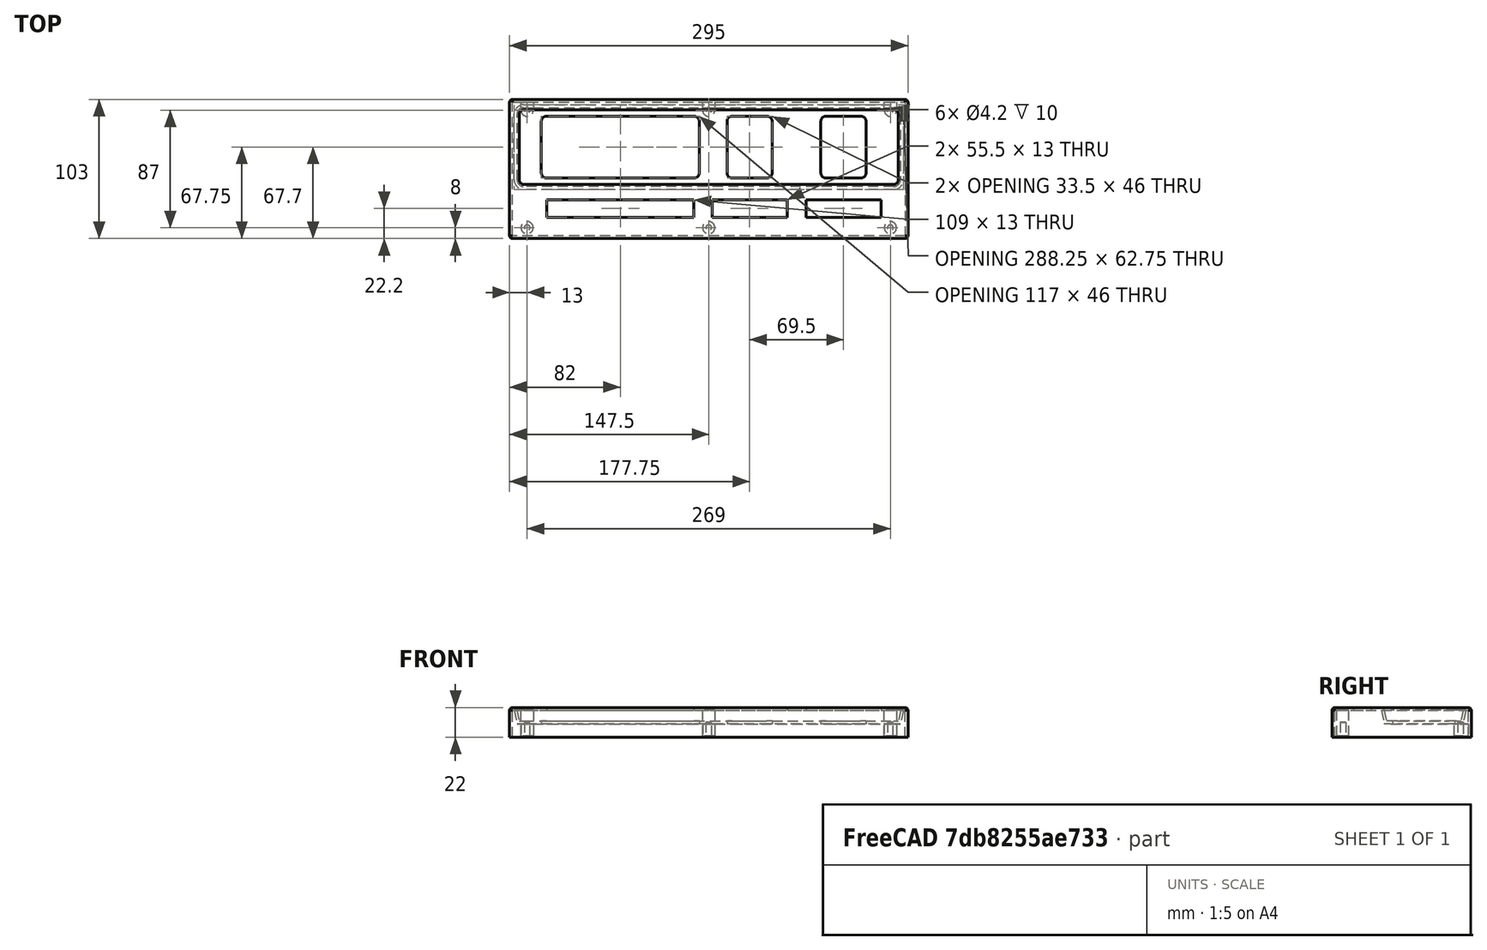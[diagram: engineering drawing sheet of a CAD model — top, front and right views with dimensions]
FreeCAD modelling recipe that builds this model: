
FCSTD DOCUMENT  (FreeCAD 0.21R33771 (Git))
Label: front panel
License: All rights reserved
LicenseURL: http://en.wikipedia.org/wiki/All_rights_reserved
objects: Sketcher::SketchObject×6, PartDesign::LinearPattern×4, PartDesign::Pad×3, PartDesign::Pocket×3, TechDraw::DrawViewDimension×3, PartDesign::Draft×1, PartDesign::Thickness×1, PartDesign::MultiTransform×1, PartDesign::Body×1, TechDraw::DrawSVGTemplate×1, TechDraw::DrawProjGroupItem×1, TechDraw::DrawProjGroup×1, TechDraw::DrawPage×1
note: 33 computed .brp shape members not serialized (recipe doc carries the construction recipe); baked Part::Feature solids carry a one-line shape summary decoded from their .brp

FEATURE [Sketcher::SketchObject] Sketch
  FullyConstrained = true
  MapMode = 5
  Support = -> [XY_Plane]
  sketch-geometry (4):
    g0: LineSegment StartX=-145.5 StartY=49.5 StartZ=0 EndX=145.5 EndY=49.5 EndZ=0
    g1: LineSegment StartX=145.5 StartY=49.5 StartZ=0 EndX=145.5 EndY=-49.5 EndZ=0
    g2: LineSegment StartX=145.5 StartY=-49.5 StartZ=0 EndX=-145.5 EndY=-49.5 EndZ=0
    g3: LineSegment StartX=-145.5 StartY=-49.5 StartZ=0 EndX=-145.5 EndY=49.5 EndZ=0
  constraints (11):
    c: Coincident(g0,g1)
    c: Coincident(g1,g2)
    c: Coincident(g2,g3)
    c: Coincident(g3,g0)
    c: Horizontal(g0)
    c: Horizontal(g2)
    c: Vertical(g1)
    c: Vertical(g3)
    c: Symmetric(g1,g0,g-1)
    c: DistanceY(g3,g3) = 99
    c: DistanceX(g0,g0) = 291
FEATURE [PartDesign::Pad] Pad
  Direction = (0,0,1)
  Length = 20
  Length2 = 10
  Profile = -> Sketch
  ReferenceAxis = -> Sketch [N_Axis]
  Type = 0
FEATURE [Sketcher::SketchObject] Sketch001
  FullyConstrained = true
  MapMode = 5
  Placement = pos=(0,0,20) rot=(0,0,1;0rad)
  Support = -> [Pad]
  sketch-geometry (10):
    g0: ArcOfCircle CenterX=-137 CenterY=40.5 CenterZ=0 NormalX=0 NormalY=0 NormalZ=1 AngleXU=0 Radius=5 StartAngle=1.5708 EndAngle=3.14159
    g1: LineSegment StartX=-137 StartY=45.5 StartZ=0 EndX=137 EndY=45.5 EndZ=0
    g2: ArcOfCircle CenterX=137 CenterY=40.5 CenterZ=0 NormalX=0 NormalY=0 NormalZ=1 AngleXU=0 Radius=5 StartAngle=5e-16 EndAngle=1.5708
    g3: LineSegment StartX=142 StartY=40.5 StartZ=0 EndX=142 EndY=-8 EndZ=0
    g4: ArcOfCircle CenterX=137 CenterY=-8 CenterZ=0 NormalX=0 NormalY=0 NormalZ=1 AngleXU=0 Radius=5 StartAngle=4.71239 EndAngle=6.28319
    g5: LineSegment StartX=137 StartY=-13 StartZ=0 EndX=-137 EndY=-13 EndZ=0
    g6: ArcOfCircle CenterX=-137 CenterY=-8 CenterZ=0 NormalX=0 NormalY=0 NormalZ=1 AngleXU=0 Radius=5 StartAngle=3.14159 EndAngle=4.71239
    g7: LineSegment StartX=-142 StartY=-8 StartZ=0 EndX=-142 EndY=40.5 EndZ=0
    g8: GeomPoint X=-142 Y=45.5 Z=0
    g9: GeomPoint X=142 Y=-13 Z=0
  constraints (23):
    c: Tangent(g0,g1) = 1.5708
    c: Tangent(g1,g2) = 1.5708
    c: Tangent(g2,g3) = 1.5708
    c: Tangent(g3,g4) = 1.5708
    c: Tangent(g4,g5) = 1.5708
    c: Tangent(g5,g6) = 1.5708
    c: Tangent(g6,g7) = 1.5708
    c: Tangent(g7,g0) = 1.5708
    c: Horizontal(g1)
    c: Horizontal(g5)
    c: Vertical(g3)
    c: Vertical(g7)
    c: Equal(g2,g4)
    c: Equal(g4,g6)
    c: PointOnObject(g8,g1)
    c: PointOnObject(g8,g7)
    c: PointOnObject(g9,g3)
    c: PointOnObject(g9,g5)
    c: Diameter(g2) = 10
    c: DistanceX(g0,g2) = 284
    c: Symmetric(g0,g2,g-2)
    c: DistanceY(g-1,g0) = 45.5
    c: DistanceY(g5,g-1) = 13
FEATURE [PartDesign::Pocket] Pocket
  BaseFeature = -> Pad
  Direction = (0,0,-1)
  Length = 10
  Length2 = 5
  Profile = -> Sketch001
  ReferenceAxis = -> Sketch001 [N_Axis]
  Type = 0
FEATURE [PartDesign::Draft] Draft
  Angle = 12
  Base = -> Pocket [Face10]
  BaseFeature = -> Pocket
  NeutralPlane = -> Pocket [Face15]
  SupportTransform = false
FEATURE [PartDesign::Thickness] Thickness
  Base = -> Draft [Face4]
  BaseFeature = -> Draft
  Intersection = false
  Join = 0
  Mode = 0
  SupportTransform = false
  Value = 2
FEATURE [Sketcher::SketchObject] Sketch002
  FullyConstrained = true
  MapMode = 5
  Placement = pos=(0,0,22) rot=(0,0,1;0rad)
  Support = -> [Thickness]
  sketch-geometry (42):
    g0: LineSegment StartX=-120 StartY=-22.8 StartZ=0 EndX=-11 EndY=-22.8 EndZ=0
    g1: LineSegment StartX=-11 StartY=-22.8 StartZ=0 EndX=-11 EndY=-35.8 EndZ=0
    g2: LineSegment StartX=-11 StartY=-35.8 StartZ=0 EndX=-120 EndY=-35.8 EndZ=0
    g3: LineSegment StartX=-120 StartY=-35.8 StartZ=0 EndX=-120 EndY=-22.8 EndZ=0
    g4: LineSegment StartX=2.5 StartY=-22.8 StartZ=0 EndX=58 EndY=-22.8 EndZ=0
    g5: LineSegment StartX=58 StartY=-22.8 StartZ=0 EndX=58 EndY=-35.8 EndZ=0
    g6: LineSegment StartX=58 StartY=-35.8 StartZ=0 EndX=2.5 EndY=-35.8 EndZ=0
    g7: LineSegment StartX=2.5 StartY=-35.8 StartZ=0 EndX=2.5 EndY=-22.8 EndZ=0
    g8: LineSegment StartX=72 StartY=-22.8 StartZ=0 EndX=127.5 EndY=-22.8 EndZ=0
    g9: LineSegment StartX=127.5 StartY=-22.8 StartZ=0 EndX=127.5 EndY=-35.8 EndZ=0
    g10: LineSegment StartX=127.5 StartY=-35.8 StartZ=0 EndX=72 EndY=-35.8 EndZ=0
    g11: LineSegment StartX=72 StartY=-35.8 StartZ=0 EndX=72 EndY=-22.8 EndZ=0
    g12: ArcOfCircle CenterX=-120 CenterY=35.2 CenterZ=0 NormalX=0 NormalY=0 NormalZ=1 AngleXU=0 Radius=4 StartAngle=1.5708 EndAngle=3.14159
    g13: LineSegment StartX=-120 StartY=39.2 StartZ=0 EndX=-11 EndY=39.2 EndZ=0
    g14: ArcOfCircle CenterX=-11 CenterY=35.2 CenterZ=0 NormalX=0 NormalY=0 NormalZ=1 AngleXU=0 Radius=4 StartAngle=1e-16 EndAngle=1.5708
    g15: LineSegment StartX=-7 StartY=35.2 StartZ=0 EndX=-7 EndY=-2.8 EndZ=0
    g16: ArcOfCircle CenterX=-11 CenterY=-2.8 CenterZ=0 NormalX=0 NormalY=0 NormalZ=1 AngleXU=0 Radius=4 StartAngle=4.71239 EndAngle=6.28319
    g17: LineSegment StartX=-11 StartY=-6.8 StartZ=0 EndX=-120 EndY=-6.8 EndZ=0
    g18: ArcOfCircle CenterX=-120 CenterY=-2.8 CenterZ=0 NormalX=0 NormalY=0 NormalZ=1 AngleXU=0 Radius=4 StartAngle=3.14159 EndAngle=4.71239
    g19: LineSegment StartX=-124 StartY=-2.8 StartZ=0 EndX=-124 EndY=35.2 EndZ=0
    g20: GeomPoint X=-124 Y=39.2 Z=0
    g21: GeomPoint X=-7 Y=-6.8 Z=0
    g22: ArcOfCircle CenterX=17.5 CenterY=35.2 CenterZ=0 NormalX=0 NormalY=0 NormalZ=1 AngleXU=0 Radius=4 StartAngle=1.5708 EndAngle=3.14159
    g23: LineSegment StartX=17.5 StartY=39.2 StartZ=0 EndX=43 EndY=39.2 EndZ=0
    g24: ArcOfCircle CenterX=43 CenterY=35.2 CenterZ=0 NormalX=0 NormalY=0 NormalZ=1 AngleXU=0 Radius=4 StartAngle=0 EndAngle=1.5708
    g25: LineSegment StartX=47 StartY=35.2 StartZ=0 EndX=47 EndY=-2.8 EndZ=0
    g26: ArcOfCircle CenterX=43 CenterY=-2.8 CenterZ=0 NormalX=0 NormalY=0 NormalZ=1 AngleXU=0 Radius=4 StartAngle=4.71239 EndAngle=6.28319
    g27: LineSegment StartX=43 StartY=-6.8 StartZ=0 EndX=17.5 EndY=-6.8 EndZ=0
    g28: ArcOfCircle CenterX=17.5 CenterY=-2.8 CenterZ=0 NormalX=0 NormalY=0 NormalZ=1 AngleXU=0 Radius=4 StartAngle=3.14159 EndAngle=4.71239
    g29: LineSegment StartX=13.5 StartY=-2.8 StartZ=0 EndX=13.5 EndY=35.2 EndZ=0
    g30: GeomPoint X=13.5 Y=39.2 Z=0
    g31: GeomPoint X=47 Y=-6.8 Z=0
    g32: ArcOfCircle CenterX=87 CenterY=35.2 CenterZ=0 NormalX=0 NormalY=0 NormalZ=1 AngleXU=0 Radius=4 StartAngle=1.5708 EndAngle=3.14159
    g33: LineSegment StartX=87 StartY=39.2 StartZ=0 EndX=112.5 EndY=39.2 EndZ=0
    g34: ArcOfCircle CenterX=112.5 CenterY=35.2 CenterZ=0 NormalX=0 NormalY=0 NormalZ=1 AngleXU=0 Radius=4 StartAngle=1e-16 EndAngle=1.5708
    g35: LineSegment StartX=116.5 StartY=35.2 StartZ=0 EndX=116.5 EndY=-2.8 EndZ=0
    g36: ArcOfCircle CenterX=112.5 CenterY=-2.8 CenterZ=0 NormalX=0 NormalY=0 NormalZ=1 AngleXU=0 Radius=4 StartAngle=4.71239 EndAngle=6.28319
    g37: LineSegment StartX=112.5 StartY=-6.8 StartZ=0 EndX=87 EndY=-6.8 EndZ=0
    g38: ArcOfCircle CenterX=87 CenterY=-2.8 CenterZ=0 NormalX=0 NormalY=0 NormalZ=1 AngleXU=0 Radius=4 StartAngle=3.14159 EndAngle=4.71239
    g39: LineSegment StartX=83 StartY=-2.8 StartZ=0 EndX=83 EndY=35.2 EndZ=0
    g40: GeomPoint X=83 Y=39.2 Z=0
    g41: GeomPoint X=116.5 Y=-6.8 Z=0
  constraints (108):
    c: Coincident(g0,g1)
    c: Coincident(g1,g2)
    c: Coincident(g2,g3)
    c: Coincident(g3,g0)
    c: Horizontal(g0)
    c: Horizontal(g2)
    c: Vertical(g1)
    c: Vertical(g3)
    c: Coincident(g4,g5)
    c: Coincident(g5,g6)
    c: Coincident(g6,g7)
    c: Coincident(g7,g4)
    c: Horizontal(g4)
    c: Horizontal(g6)
    c: Vertical(g5)
    c: Vertical(g7)
    c: Coincident(g8,g9)
    c: Coincident(g9,g10)
    c: Coincident(g10,g11)
    c: Coincident(g11,g8)
    c: Horizontal(g8)
    c: Horizontal(g10)
    c: Vertical(g9)
    c: Vertical(g11)
    c: Horizontal(g10,g5)
    c: Horizontal(g5,g1)
    c: Horizontal(g4,g0)
    c: Horizontal(g0,g8)
    c: DistanceY(g3,g3) = 13
    c: DistanceX(g2,g-1) = 120
    c: DistanceX(g0,g0) = 109
    c: DistanceY(g1,g-1) = 35.8
    c: DistanceX(g0,g4) = 13.5
    c: DistanceX(g4,g4) = 55.5
    c: DistanceX(g4,g8) = 14
    c: Equal(g8,g4)
    c: Tangent(g12,g13) = 1.5708
    c: Tangent(g13,g14) = 1.5708
    c: Tangent(g14,g15) = 1.5708
    c: Tangent(g15,g16) = 1.5708
    c: Tangent(g16,g17) = 1.5708
    c: Tangent(g17,g18) = 1.5708
    c: Tangent(g18,g19) = 1.5708
    c: Tangent(g19,g12) = 1.5708
    c: Horizontal(g13)
    c: Horizontal(g17)
    c: Vertical(g15)
    c: Vertical(g19)
    c: Equal(g12,g14)
    c: Equal(g14,g16)
    c: Equal(g16,g18)
    c: PointOnObject(g20,g13)
    c: PointOnObject(g20,g19)
    c: PointOnObject(g21,g15)
    c: PointOnObject(g21,g17)
    c: Radius(g12) = 4
    c: Vertical(g17,g0)
    c: Vertical(g16,g0)
    c: Tangent(g22,g23) = 1.5708
    c: Tangent(g23,g24) = 1.5708
    c: Tangent(g24,g25) = 1.5708
    c: Tangent(g25,g26) = 1.5708
    c: Tangent(g26,g27) = 1.5708
    c: Tangent(g27,g28) = 1.5708
    c: Tangent(g28,g29) = 1.5708
    c: Tangent(g29,g22) = 1.5708
    c: Horizontal(g23)
    c: Horizontal(g27)
    c: Vertical(g25)
    c: Vertical(g29)
    c: Equal(g22,g24)
    c: Equal(g24,g26)
    c: Equal(g26,g28)
    c: PointOnObject(g30,g23)
    c: PointOnObject(g30,g29)
    c: PointOnObject(g31,g25)
    c: PointOnObject(g31,g27)
    c: Equal(g26,g14)
    c: Horizontal(g22,g13)
    c: Horizontal(g27,g16)
    c: DistanceX(g26,g4) = 15
    c: DistanceX(g4,g27) = 15
    c: Tangent(g32,g33) = 1.5708
    c: Tangent(g33,g34) = 1.5708
    c: Tangent(g34,g35) = 1.5708
    c: Tangent(g35,g36) = 1.5708
    c: Tangent(g36,g37) = 1.5708
    c: Tangent(g37,g38) = 1.5708
    c: Tangent(g38,g39) = 1.5708
    c: Tangent(g39,g32) = 1.5708
    c: Horizontal(g33)
    c: Horizontal(g37)
    c: Vertical(g35)
    c: Vertical(g39)
    c: Equal(g32,g34)
    c: Equal(g34,g36)
    c: Equal(g36,g38)
    c: PointOnObject(g40,g33)
    c: PointOnObject(g40,g39)
    c: PointOnObject(g41,g35)
    c: PointOnObject(g41,g37)
    c: Horizontal(g23,g32)
    c: Equal(g32,g24)
    c: DistanceX(g36,g8) = 15
    c: Equal(g27,g37)
    c: DistanceY(g8,g35) = 20
    c: DistanceY(g8,g33) = 62
    c: Horizontal(g37,g16)
FEATURE [PartDesign::Pocket] Pocket001
  BaseFeature = -> Thickness
  Direction = (0,0,-1)
  Length = 5
  Length2 = 5
  Profile = -> Sketch002
  ReferenceAxis = -> Sketch002 [N_Axis]
  Type = 1
FEATURE [Sketcher::SketchObject] Sketch003
  FullyConstrained = true
  MapMode = 5
  Placement = pos=(0,0,20) rot=(1,0,0;3.14159rad)
  Support = -> [Pocket001]
  sketch-geometry (1):
    g0: Circle CenterX=-134.5 CenterY=43.5 CenterZ=0 NormalX=0 NormalY=0 NormalZ=1 AngleXU=0 Radius=4.5
  constraints (3):
    c: DistanceY(g-1,g0) = 43.5
    c: DistanceX(g0,g-1) = 134.5
    c: Diameter(g0) = 9
FEATURE [PartDesign::Pad] Pad001
  BaseFeature = -> Pocket001
  Direction = (0,0,-1)
  Length = 19
  Length2 = 10
  Profile = -> Sketch003
  ReferenceAxis = -> Sketch003 [N_Axis]
  Type = 0
FEATURE [PartDesign::LinearPattern] LinearPattern
  BaseFeature = -> Pad001
  Direction = -> Sketch003 [H_Axis]
  Length = 269
  Occurrences = 3
  Originals = -> [Pad001]
FEATURE [Sketcher::SketchObject] Sketch004
  ExternalGeometry = -> [LinearPattern]
  FullyConstrained = true
  MapMode = 5
  Placement = pos=(0,0,10) rot=(1,0,0;3.14159rad)
  Support = -> [LinearPattern]
  sketch-geometry (4):
    g0: ArcOfCircle CenterX=-134.5 CenterY=-43.5 CenterZ=0 NormalX=0 NormalY=0 NormalZ=1 AngleXU=0 Radius=4.5 StartAngle=-9e-16 EndAngle=3.14159
    g1: LineSegment StartX=-139 StartY=-43.5 StartZ=0 EndX=-139 EndY=-49.5 EndZ=0
    g2: LineSegment StartX=-139 StartY=-49.5 StartZ=0 EndX=-130 EndY=-49.5 EndZ=0
    g3: LineSegment StartX=-130 StartY=-49.5 StartZ=0 EndX=-130 EndY=-43.5 EndZ=0
  constraints (11):
    c: Tangent(g0,g1) = -1.5708
    c: Coincident(g1,g2)
    c: PointOnObject(g2,g-3)
    c: Horizontal(g2)
    c: Coincident(g2,g3)
    c: Vertical(g3)
    c: Vertical(g1)
    c: Diameter(g0) = 9
    c: DistanceX(g0,g-1) = 134.5
    c: DistanceY(g0,g-1) = 43.5
    c: Tangent(g3,g0) = -1.5708
FEATURE [PartDesign::Pad] Pad002
  BaseFeature = -> LinearPattern
  Direction = (0,0,-1)
  Length = 9
  Length2 = 10
  Profile = -> Sketch004
  ReferenceAxis = -> Sketch004 [N_Axis]
  Type = 0
FEATURE [PartDesign::LinearPattern] LinearPattern001
  BaseFeature = -> Pad002
  Direction = -> Sketch004 [H_Axis]
  Length = 269
  Occurrences = 3
  Originals = -> [Pad002]
FEATURE [Sketcher::SketchObject] Sketch005
  ExternalGeometry = -> [LinearPattern001]
  FullyConstrained = true
  MapMode = 5
  Placement = pos=(0,0,1) rot=(1,0,0;3.14159rad)
  Support = -> [LinearPattern001]
  sketch-geometry (1):
    g0: Circle CenterX=-134.5 CenterY=43.5 CenterZ=0 NormalX=0 NormalY=0 NormalZ=1 AngleXU=0 Radius=2.1
  constraints (2):
    c: Coincident(g0,g-3)
    c: Diameter(g0) = 4.2
FEATURE [PartDesign::Pocket] Pocket002
  BaseFeature = -> LinearPattern001
  Direction = (0,0,1)
  Length = 10
  Length2 = 5
  Profile = -> Sketch005
  ReferenceAxis = -> Sketch005 [N_Axis]
  Type = 0
FEATURE [PartDesign::LinearPattern] LinearPattern002
  Direction = -> Sketch005 [H_Axis]
  Length = 269
  Occurrences = 3
FEATURE [PartDesign::LinearPattern] LinearPattern003
  Direction = -> Sketch005 [V_Axis]
  Length = 87
  Occurrences = 2
  Reversed = true
FEATURE [PartDesign::MultiTransform] MultiTransform
  BaseFeature = -> Pocket002
  Originals = -> [Pocket002]
  Transformations = -> [LinearPattern002,LinearPattern003]
FEATURE [PartDesign::Body] Body
  Group = -> [Sketch,Pad,Sketch001,Pocket,Draft,Thickness,Sketch002,Pocket001,Sketch003,Pad001,LinearPattern,Sketch004,Pad002,LinearPattern001,Sketch005,Pocket002,MultiTransform,LinearPattern002,LinearPattern003]
  Origin = -> Origin
  Tip = -> MultiTransform
FEATURE [TechDraw::DrawSVGTemplate] Template
  EditableTexts = APPROVER_NAME=APPROVER NAME; AUTHOR_NAME=AUTHOR NAME; DATE=YYYY-MM-DD; DN=DN; DOCUMENT_TYPE=Mechanical assembly drawing; OWNER_NAME=OWNER NAME; PM=PM; PN=PN; REVISION=REV A; RIGHTS=(R) DO NOT DUPLICATE THIS DRAWING TO THIRD PARTIES WITHOUT OWNER'S PERMISSION!; SCALE=M x:x; SHEET=99 of 99; SIZE=A3; TITLELINE-1=FreeCAD; TOLERANCE=+/- ?
  Height = 297
  Orientation = 1
  Template = /Applications/FreeCAD.app/Contents/Resources/share/Mod/TechDraw/Templates/A3_Landscape_ISO7200_Pep.svg
  Width = 420
FEATURE [TechDraw::DrawProjGroupItem] ProjItem  label="Front"
  CoarseView = false
  Direction = (0,0,1)
  Focus = 100
  HardHidden = false
  IsoCount = 0
  IsoHidden = false
  IsoVisible = false
  LockPosition = true
  Perspective = false
  Rotation = 0
  RotationVector = (1,0,0)
  ScaleType = 2
  ScrubCount = 0
  SeamHidden = false
  SeamVisible = true
  SmoothHidden = false
  SmoothVisible = true
  Source = -> [Body]
  Type = 0
  X = 0
  XDirection = (1,0,0)
  Y = 0
FEATURE [TechDraw::DrawProjGroup] ProjGroup
  Anchor = -> ProjItem
  AutoDistribute = true
  LockPosition = false
  ProjectionType = 0
  Rotation = 0
  ScaleType = 0
  Source = -> [Body]
  Views = -> [ProjItem]
  X = 210
  Y = 148.5
  spacingX = 15
  spacingY = 15
FEATURE [TechDraw::DrawViewDimension] Dimension
  AngleOverride = false
  Arbitrary = false
  ArbitraryTolerances = false
  EqualTolerance = true
  ExtensionAngle = 0
  FormatSpec = %.3f
  FormatSpecOverTolerance = %+.3f
  FormatSpecUnderTolerance = %+.3f
  Inverted = false
  LineAngle = 0
  LockPosition = false
  MeasureType = 1
  OverTolerance = 0
  References2D = -> [ProjItem]
  Rotation = 0
  ScaleType = 0
  TheoreticalExact = false
  Type = 1
  UnderTolerance = 0
  X = -2.31406
  Y = 78.7935
FEATURE [TechDraw::DrawViewDimension] Dimension001
  AngleOverride = false
  Arbitrary = false
  ArbitraryTolerances = false
  EqualTolerance = true
  ExtensionAngle = 0
  FormatSpec = %.3f
  FormatSpecOverTolerance = %+.3f
  FormatSpecUnderTolerance = %+.3f
  Inverted = false
  LineAngle = 0
  LockPosition = false
  MeasureType = 1
  OverTolerance = 0
  References2D = -> [ProjItem]
  Rotation = 0
  ScaleType = 0
  TheoreticalExact = false
  Type = 2
  UnderTolerance = 0
  X = 168.608
  Y = 20.4136
FEATURE [TechDraw::DrawViewDimension] Dimension002
  AngleOverride = false
  Arbitrary = false
  ArbitraryTolerances = false
  EqualTolerance = true
  ExtensionAngle = 0
  FormatSpec = R%.3f
  FormatSpecOverTolerance = %+.3f
  FormatSpecUnderTolerance = %+.3f
  Inverted = false
  LineAngle = 0
  LockPosition = false
  MeasureType = 1
  OverTolerance = 0
  References2D = -> [ProjItem]
  Rotation = 0
  ScaleType = 0
  TheoreticalExact = false
  Type = 4
  UnderTolerance = 0
  X = -162.459
  Y = 43.8237
FEATURE [TechDraw::DrawPage] Page
  KeepUpdated = true
  NextBalloonIndex = 1
  ProjectionType = 0
  Template = -> Template
  Views = -> [ProjGroup,Dimension,Dimension001,Dimension002]
